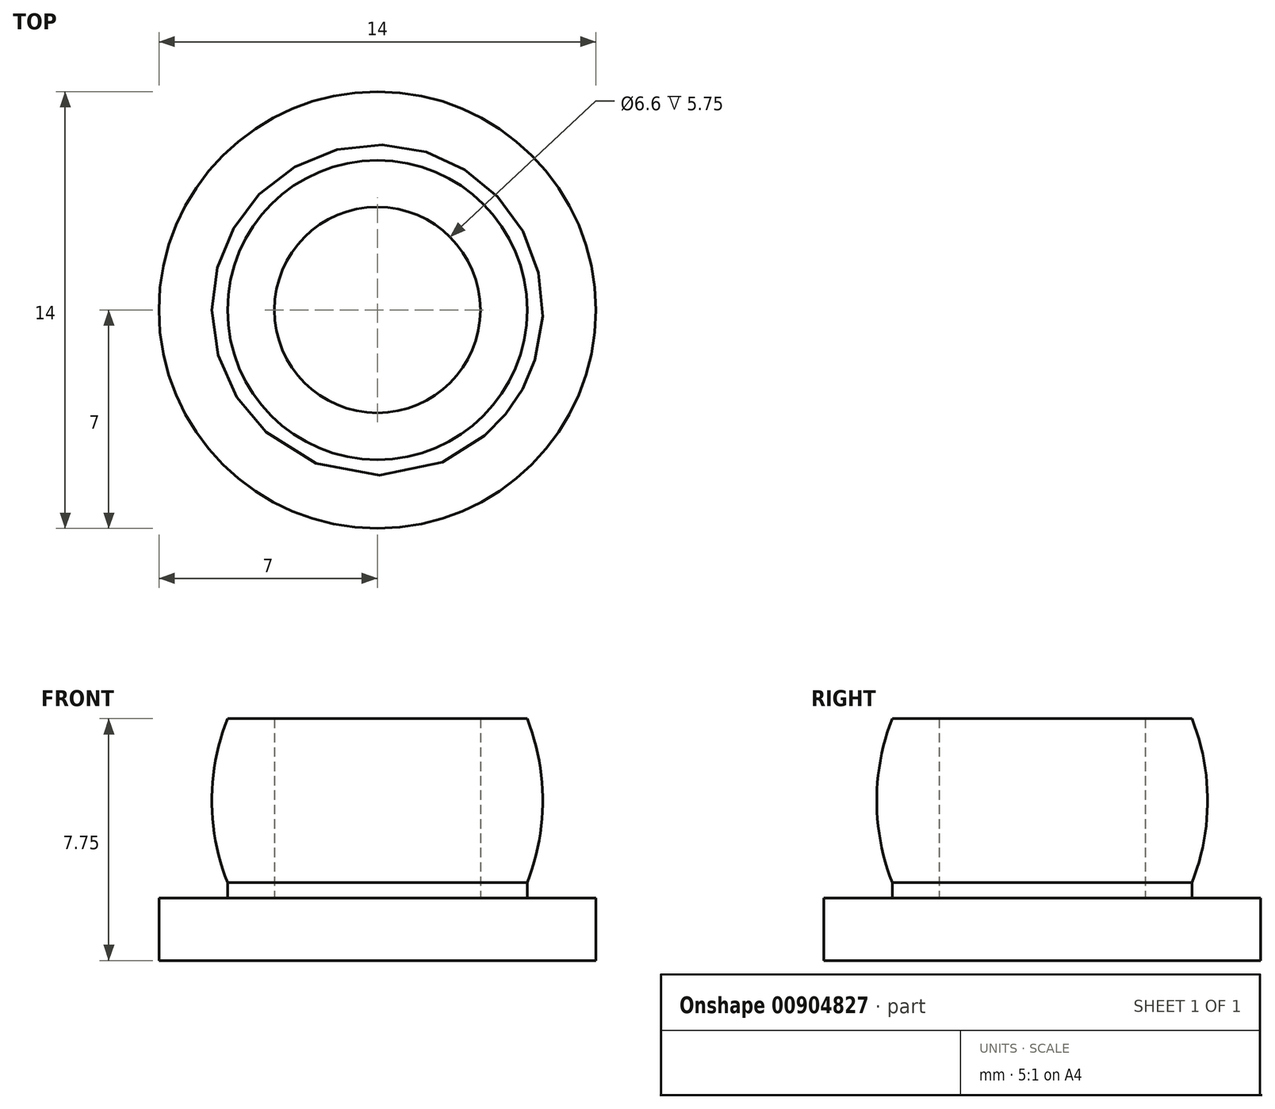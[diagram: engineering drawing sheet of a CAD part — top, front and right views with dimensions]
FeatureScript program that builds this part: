
annotation { "Feature Type Name" : "Feature", "Feature Type Description" : "" }
export const myFeature = defineFeature(function(context is Context, id is Id, definition is map)
    precondition{}
    {
        {
            var Q0;
            Q0=qCreatedBy(makeId("Front.planeOp"),FACE);
            var sketch = newSketch(context, id + "F0", { "sketchPlane" : qUnion([Q0])});
            skLineSegment(sketch, "E0", {"start": v(0, 0) * mm, "end": v(7, 0) * mm});
            skLineSegment(sketch, "E1", {"start": v(7, 0) * mm, "end": v(7, 2) * mm});
            skLineSegment(sketch, "E2", {"start": v(7, 2) * mm, "end": v(4.8, 2) * mm});
            skLineSegment(sketch, "E3", {"start": v(0, 0) * mm, "end": v(0, 2) * mm});
            skLineSegment(sketch, "E4", {"start": v(3.3, 7.75) * mm, "end": v(4.8, 7.75) * mm});
            skLineSegment(sketch, "E5", {"start": v(4.8, 2) * mm, "end": v(4.8, 2.5) * mm});
            skArc(sketch, "E6", {"start": v(4.8, 2.5) * mm, "mid": v(5.3, 5.12) * mm, "end": v(4.8, 7.75) * mm});
            skLineSegment(sketch, "E7", {"start": v(0, 2) * mm, "end": v(3.3, 2) * mm});
            skLineSegment(sketch, "E8", {"start": v(3.3, 2) * mm, "end": v(3.3, 7.75) * mm});
            skSolve(sketch);
        }
        {
            var Q0;
            Q0=makeQuery(id+"F0.imprint","IMPRINT",FACE,{"disambiguationData":[TD([[makeQuery(id+"F0.imprint","IMPRINT",EDGE,{"derivedFrom":sQuery(id+"F0.wireOp",EDGE,"E0")}),1.0]])]});
            var Q1;
            Q1=sQuery(id+"F0.wireOp",EDGE,"E3");
            revolve(context, id + "F1", {"surfaceOperationType" : NewSurfaceOperationType.NEW, "entities" : qUnion([Q0]), "axis" : qUnion([Q1]), "revolveType" : RevolveType.FULL});
        }
    });
